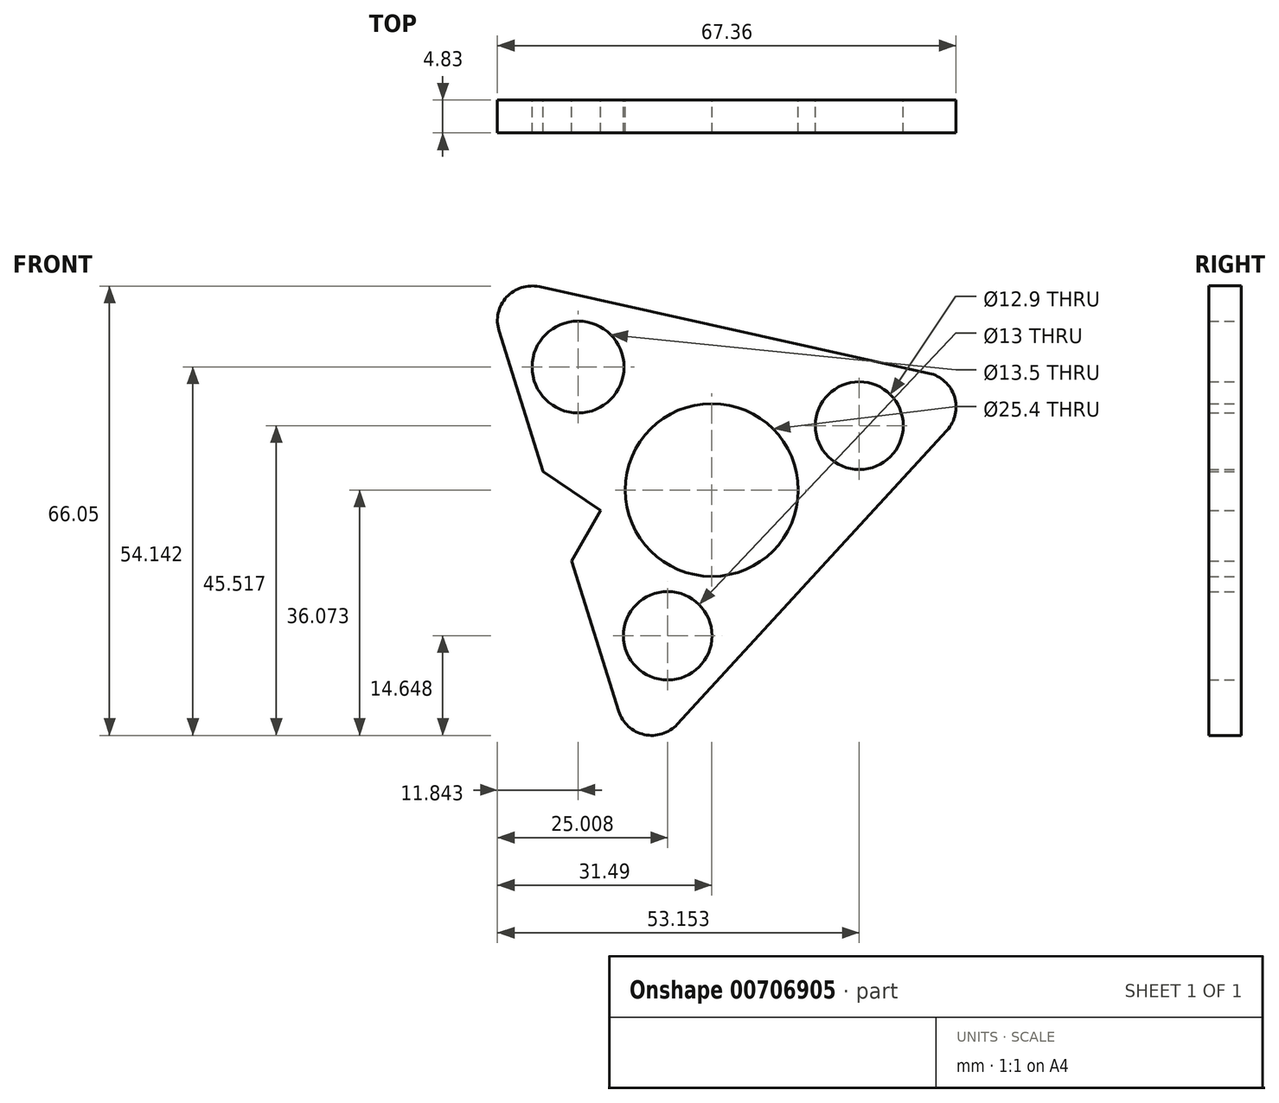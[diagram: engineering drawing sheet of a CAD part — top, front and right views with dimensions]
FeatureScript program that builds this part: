
annotation { "Feature Type Name" : "Feature", "Feature Type Description" : "" }
export const myFeature = defineFeature(function(context is Context, id is Id, definition is map)
    precondition{}
    {
        {
            var Q0;
            Q0=qCreatedBy(makeId("Front.planeOp"),FACE);
            var sketch = newSketch(context, id + "F0", { "sketchPlane" : qUnion([Q0])});
            skLineSegment(sketch, "E0", {"start": v(0, -222.07) * mm, "end": v(51.5, -165.91) * mm});
            skLineSegment(sketch, "E1", {"start": v(51.5, -165.91) * mm, "end": v(-22.88, -149.39) * mm});
            skLineSegment(sketch, "E2", {"start": v(-22.88, -149.39) * mm, "end": v(0, -222.07) * mm});
            skCircle(sketch, "E3", {"center": v(11.02, -181.16) * mm, "radius": 12.7 * mm});
            skCircle(sketch, "E4", {"center": v(32.68, -171.71) * mm, "radius": 6.45 * mm});
            skCircle(sketch, "E5", {"center": v(4.54, -202.58) * mm, "radius": 6.5 * mm});
            skCircle(sketch, "E6", {"center": v(-8.63, -163.09) * mm, "radius": 6.75 * mm});
            skLineSegment(sketch, "E7", {"start": v(20.98, -189.04) * mm, "end": v(20.98, -199.2) * mm});
            skLineSegment(sketch, "E8", {"start": v(-5.33, -184.14) * mm, "end": v(-9.6, -191.57) * mm});
            skLineSegment(sketch, "E9", {"start": v(-9.6, -191.57) * mm, "end": v(-13.74, -178.43) * mm});
            skLineSegment(sketch, "E10", {"start": v(-13.74, -178.43) * mm, "end": v(-5.33, -184.14) * mm});
            skSolve(sketch);
        }
        {
            var Q0;
            Q0=makeQuery(id+"F0.imprint","IMPRINT",FACE,{"disambiguationData":[TD([[makeQuery(id+"F0.imprint","IMPRINT",EDGE,{"derivedFrom":sQuery(id+"F0.wireOp",EDGE,"E0")}),-1.0]])]});
            var Q1;
            Q1=makeQuery(id+"F0.imprint","IMPRINT",FACE,{"disambiguationData":[TD([[makeQuery(id+"F0.imprint","IMPRINT",EDGE,{"derivedFrom":sQuery(id+"F0.wireOp",EDGE,"E0")}),1.0]])]});
            extrude(context, id + "F1", {"entities" : qUnion([Q0, Q1]), "depth" : 4.83 * mm, "offsetDistance" : 25.4 * mm});
        }
        {
            var Q0;
            Q0=makeQuery(id+"F1.opExtrude","SWEPT_EDGE",EDGE,{"disambiguationData":[OSD([sQuery(id+"F0.wireOp",EDGE,"E0"),sQuery(id+"F0.wireOp",EDGE,"E2")])]});
            var Q1;
            Q1=makeQuery(id+"F1.opExtrude","SWEPT_EDGE",EDGE,{"disambiguationData":[OSD([sQuery(id+"F0.wireOp",EDGE,"E0"),sQuery(id+"F0.wireOp",EDGE,"E1")])]});
            var Q2;
            Q2=makeQuery(id+"F1.opExtrude","SWEPT_EDGE",EDGE,{"disambiguationData":[OSD([sQuery(id+"F0.wireOp",EDGE,"E1"),sQuery(id+"F0.wireOp",EDGE,"E2")])]});
            fillet(context, id + "F2", {"entities" : qUnion([Q0, Q1, Q2]), "radius" : 5.08 * mm, "tangentPropagation" : true, "allowEdgeOverflow" : false});
        }
    });
